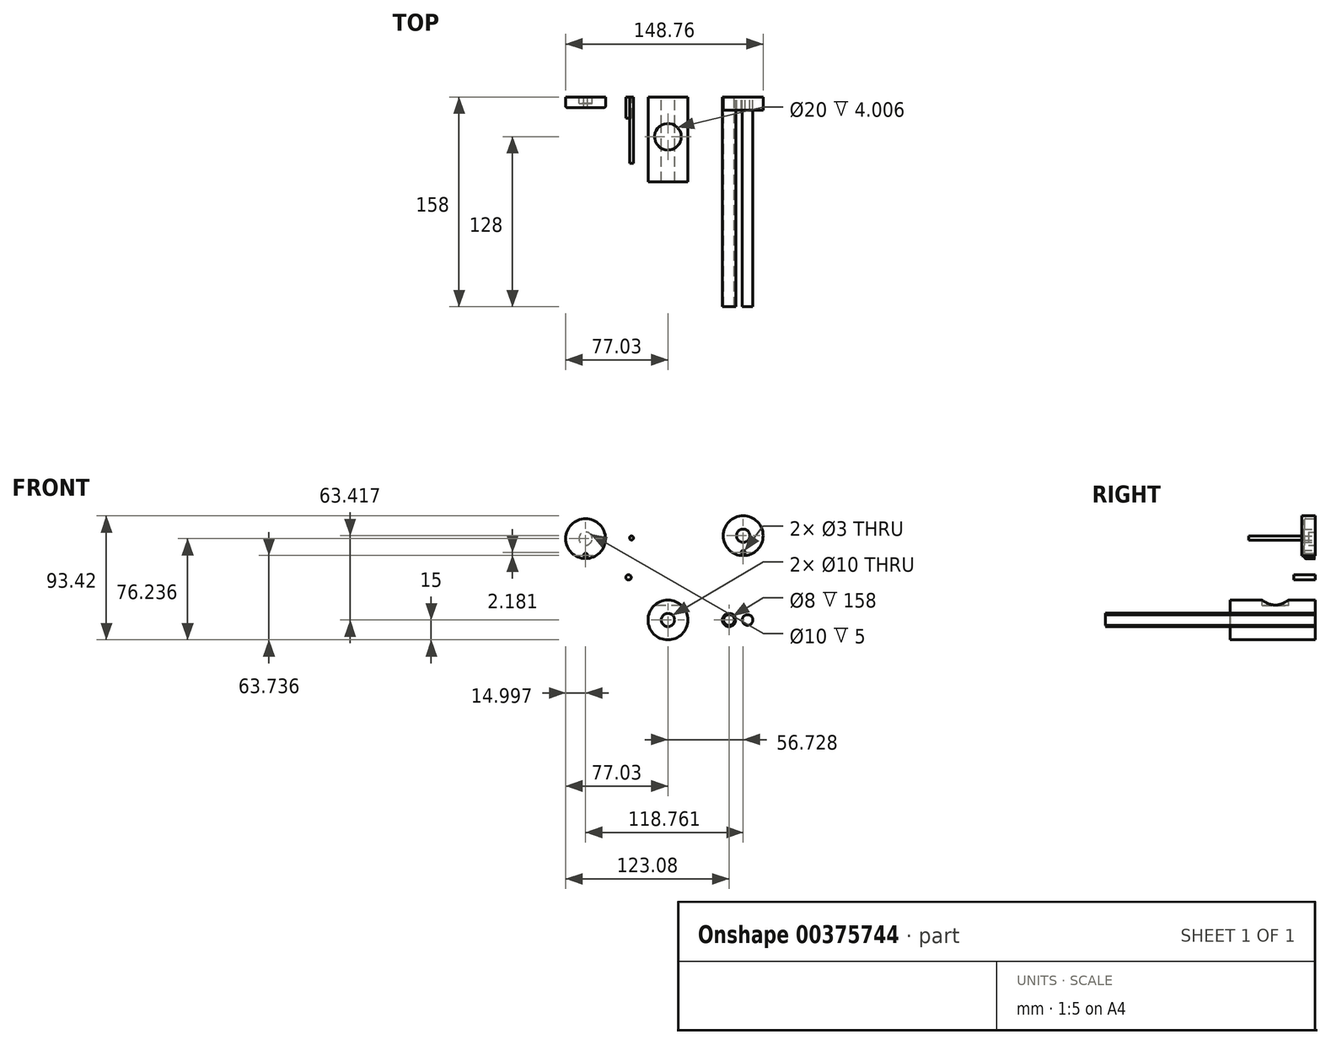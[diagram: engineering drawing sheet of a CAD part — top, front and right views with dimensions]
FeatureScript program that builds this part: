
annotation { "Feature Type Name" : "Feature", "Feature Type Description" : "" }
export const myFeature = defineFeature(function(context is Context, id is Id, definition is map)
    precondition{}
    {
        {
            var Q0;
            Q0=qCreatedBy(makeId("Front.planeOp"),FACE);
            var sketch = newSketch(context, id + "F0", { "sketchPlane" : qUnion([Q0])});
            skCircle(sketch, "E0", {"center": v(0, 0) * mm, "radius": 15 * mm});
            skCircle(sketch, "E1", {"center": v(0, 0) * mm, "radius": 5 * mm});
            skSolve(sketch);
        }
        {
            var Q0;
            Q0=qSketchRegion(id+"F0",true);
            extrude(context, id + "F1", {"entities" : qUnion([Q0]), "depth" : 64 * mm});
        }
        {
            var Q0;
            Q0=qCreatedBy(makeId("Front.planeOp"),FACE);
            var sketch = newSketch(context, id + "F2", { "sketchPlane" : qUnion([Q0])});
            skArc(sketch, "E2", {"start": v(-51.43, 3.76) * mm, "mid": v(-62.22, 29.18) * mm, "end": v(-73, 3.76) * mm});
            skCircle(sketch, "E3", {"center": v(-62.22, 14.18) * mm, "radius": 5 * mm});
            skCircle(sketch, "E4", {"center": v(-72.22, 14.18) * mm, "radius": 2 * mm});
            skCircle(sketch, "E5", {"center": v(-52.22, 14.18) * mm, "radius": 2 * mm});
            skLineSegment(sketch, "E6", {"start": v(-54.3, 6.54) * mm, "end": v(-51.43, 3.76) * mm});
            skLineSegment(sketch, "E7", {"start": v(-70.13, 6.54) * mm, "end": v(-73, 3.76) * mm});
            skArc(sketch, "E8", {"start": v(-70.13, 6.54) * mm, "mid": v(-62.22, 3.18) * mm, "end": v(-54.3, 6.54) * mm});
            skLineSegment(sketch, "E9", {"start": v(-62.22, 14.18) * mm, "end": v(-47.22, 14.18) * mm});
            skSolve(sketch);
        }
        {
            var Q0;
            Q0=qSketchRegion(id+"F2",true);
            extrude(context, id + "F3", {"entities" : qUnion([Q0]), "depth" : 3 * mm});
        }
        {
            var Q0;
            Q0=qCreatedBy(makeId("Front.planeOp"),FACE);
            var sketch = newSketch(context, id + "F4", { "sketchPlane" : qUnion([Q0])});
            skCircle(sketch, "E10", {"center": v(-47.77, -37.5) * mm, "radius": 15 * mm});
            skCircle(sketch, "E11", {"center": v(-47.77, -37.5) * mm, "radius": 5 * mm});
            skCircle(sketch, "E12", {"center": v(-57.77, -37.5) * mm, "radius": 2 * mm});
            skCircle(sketch, "E13", {"center": v(-37.77, -37.5) * mm, "radius": 2 * mm});
            skSolve(sketch);
        }
        {
            var Q0;
            Q0=qSketchRegion(id+"F4",true);
            extrude(context, id + "F5", {"entities" : qUnion([Q0]), "depth" : 10 * mm});
        }
        {
            var Q0;
            Q0=qCreatedBy(makeId("Front.planeOp"),FACE);
            var sketch = newSketch(context, id + "F6", { "sketchPlane" : qUnion([Q0])});
            skCircle(sketch, "E14", {"center": v(12.7, 49.03) * mm, "radius": 15 * mm});
            skCircle(sketch, "E15", {"center": v(12.7, 49.03) * mm, "radius": 5 * mm});
            skCircle(sketch, "E16", {"center": v(12.7, 36.53) * mm, "radius": 1.5 * mm});
            skSolve(sketch);
        }
        {
            var Q0;
            Q0=qSketchRegion(id+"F6",true);
            extrude(context, id + "F7", {"entities" : qUnion([Q0]), "depth" : 2 * mm});
        }
        {
            var Q0;
            Q0=qCreatedBy(makeId("Top.planeOp"),FACE);
            cPlane(context, id + "F8", {"entities" : qUnion([Q0]), "cplaneType" : CPlaneType.OFFSET, "offset" : 15 * mm, "width" : 150 * mm, "height" : 150 * mm});
        }
        {
            var Q0;
            Q0=qCreatedBy(id+"F8.planeOp",FACE);
            var sketch = newSketch(context, id + "F9", { "sketchPlane" : qUnion([Q0])});
            skCircle(sketch, "E17", {"center": v(0, -30) * mm, "radius": 10 * mm});
            skSolve(sketch);
        }
        {
            var Q0;
            Q0=qSketchRegion(id+"F9",true);
            extrude(context, id + "F10", {"entities" : qUnion([Q0]), "operationType" : NewBodyOperationType.REMOVE, "oppositeDirection" : true, "depth" : 4 * mm});
        }
        {
            var Q0;
            Q0=qCreatedBy(makeId("Front.planeOp"),FACE);
            var sketch = newSketch(context, id + "F11", { "sketchPlane" : qUnion([Q0])});
            skCircle(sketch, "E18", {"center": v(46.05, 0) * mm, "radius": 5 * mm});
            skCircle(sketch, "E19", {"center": v(46.05, 0) * mm, "radius": 4 * mm});
            skSolve(sketch);
        }
        {
            var Q0;
            Q0=qSketchRegion(id+"F11",true);
            extrude(context, id + "F12", {"entities" : qUnion([Q0]), "depth" : 158 * mm});
        }
        {
            var Q0;
            Q0=qCreatedBy(makeId("Front.planeOp"),FACE);
            var sketch = newSketch(context, id + "F13", { "sketchPlane" : qUnion([Q0])});
            skCircle(sketch, "E20", {"center": v(60, 0) * mm, "radius": 4 * mm});
            skSolve(sketch);
        }
        {
            var Q0;
            Q0=qSketchRegion(id+"F13",true);
            var Q1;
            Q1=qSketchRegion(id+"F15",true);
            extrude(context, id + "F14", {"entities" : qUnion([Q0, Q1]), "depth" : 158 * mm});
        }
        {
            var Q0;
            Q0=qCreatedBy(makeId("Front.planeOp"),FACE);
            var sketch = newSketch(context, id + "F15", { "sketchPlane" : qUnion([Q0])});
            skCircle(sketch, "E21", {"center": v(-29.66, 32.1) * mm, "radius": 2 * mm});
            skSolve(sketch);
        }
        {
            var Q0;
            Q0=qSketchRegion(id+"F15",true);
            extrude(context, id + "F16", {"entities" : qUnion([Q0]), "depth" : 16 * mm});
        }
        {
            var Q0;
            Q0=qCreatedBy(makeId("Front.planeOp"),FACE);
            var sketch = newSketch(context, id + "F17", { "sketchPlane" : qUnion([Q0])});
            skCircle(sketch, "E22", {"center": v(-62.03, 61.24) * mm, "radius": 15 * mm});
            skCircle(sketch, "E23", {"center": v(-62.03, 48.74) * mm, "radius": 1.5 * mm});
            skCircle(sketch, "E24", {"center": v(56.73, 63.42) * mm, "radius": 15 * mm});
            skCircle(sketch, "E25", {"center": v(56.73, 50.92) * mm, "radius": 1.5 * mm});
            skCircle(sketch, "E26", {"center": v(56.73, 63.42) * mm, "radius": 5 * mm});
            skSolve(sketch);
        }
        {
            var Q0;
            Q0=makeQuery(id+"F17.imprint","IMPRINT",FACE,{"disambiguationData":[TD([[makeQuery(id+"F17.imprint","IMPRINT",EDGE,{"derivedFrom":sQuery(id+"F17.wireOp",EDGE,"E22")}),1.0]])]});
            extrude(context, id + "F18", {"entities" : qUnion([Q0]), "depth" : 8 * mm});
        }
        {
            var Q0;
            Q0=qCreatedBy(makeId("Front.planeOp"),FACE);
            var sketch = newSketch(context, id + "F19", { "sketchPlane" : qUnion([Q0])});
            skCircle(sketch, "E27", {"center": v(-27.45, 61.7) * mm, "radius": 1.5 * mm});
            skSolve(sketch);
        }
        {
            var Q0;
            Q0=qSketchRegion(id+"F19",true);
            extrude(context, id + "F20", {"entities" : qUnion([Q0]), "depth" : 50 * mm});
        }
        {
            var Q0;
            Q0=makeQuery(id+"F18.opExtrude","CAP_EDGE",EDGE,{"disambiguationData":[OSD([sQuery(id+"F17.wireOp",EDGE,"E22")])],"isStart":false});
            fillet(context, id + "F21", {"entities" : qUnion([Q0]), "radius" : 1 * mm, "tangentPropagation" : true, "allowEdgeOverflow" : false});
        }
        {
            var Q0;
            Q0=makeQuery(id+"F17.imprint","IMPRINT",FACE,{"disambiguationData":[TD([[makeQuery(id+"F17.imprint","IMPRINT",EDGE,{"derivedFrom":sQuery(id+"F17.wireOp",EDGE,"E24")}),1.0]])]});
            extrude(context, id + "F22", {"entities" : qUnion([Q0]), "depth" : 10 * mm});
        }
        {
            var Q0;
            Q0=makeQuery(id+"F18.opExtrude","CAP_FACE",FACE,{"disambiguationData":[OSD([sQuery(id+"F17.wireOp",EDGE,"E22"),sQuery(id+"F17.wireOp",EDGE,"E23")])],"isStart":true});
            var sketch = newSketch(context, id + "F23", { "sketchPlane" : qUnion([Q0])});
            skCircle(sketch, "E28", {"center": v(62.03, 61.24) * mm, "radius": 5 * mm});
            skSolve(sketch);
        }
        {
            var Q0;
            Q0=qSketchRegion(id+"F23",true);
            extrude(context, id + "F24", {"entities" : qUnion([Q0]), "operationType" : NewBodyOperationType.REMOVE, "oppositeDirection" : true, "depth" : 5 * mm});
        }
        {
            var Q0;
            Q0=makeQuery(id+"F3.opExtrude","SWEPT_BODY",BODY,{"disambiguationData":[OSD([sQuery(id+"F2.wireOp",EDGE,"E2"),sQuery(id+"F2.wireOp",EDGE,"E3"),sQuery(id+"F2.wireOp",EDGE,"E4"),sQuery(id+"F2.wireOp",EDGE,"E5"),sQuery(id+"F2.wireOp",EDGE,"E6"),sQuery(id+"F2.wireOp",EDGE,"E7"),sQuery(id+"F2.wireOp",EDGE,"E8")])]});
            deleteBodies(context, id + "F25", {"entities" : qUnion([Q0])});
        }
        {
            var Q0;
            Q0=makeQuery(id+"F5.opExtrude","SWEPT_BODY",BODY,{"disambiguationData":[OSD([sQuery(id+"F4.wireOp",EDGE,"E10"),sQuery(id+"F4.wireOp",EDGE,"E11"),sQuery(id+"F4.wireOp",EDGE,"E12"),sQuery(id+"F4.wireOp",EDGE,"E13")])]});
            deleteBodies(context, id + "F26", {"entities" : qUnion([Q0])});
        }
        {
            var Q0;
            Q0=makeQuery(id+"F7.opExtrude","SWEPT_BODY",BODY,{"disambiguationData":[OSD([sQuery(id+"F6.wireOp",EDGE,"E14"),sQuery(id+"F6.wireOp",EDGE,"E15"),sQuery(id+"F6.wireOp",EDGE,"E16")])]});
            deleteBodies(context, id + "F27", {"entities" : qUnion([Q0])});
        }
    });
